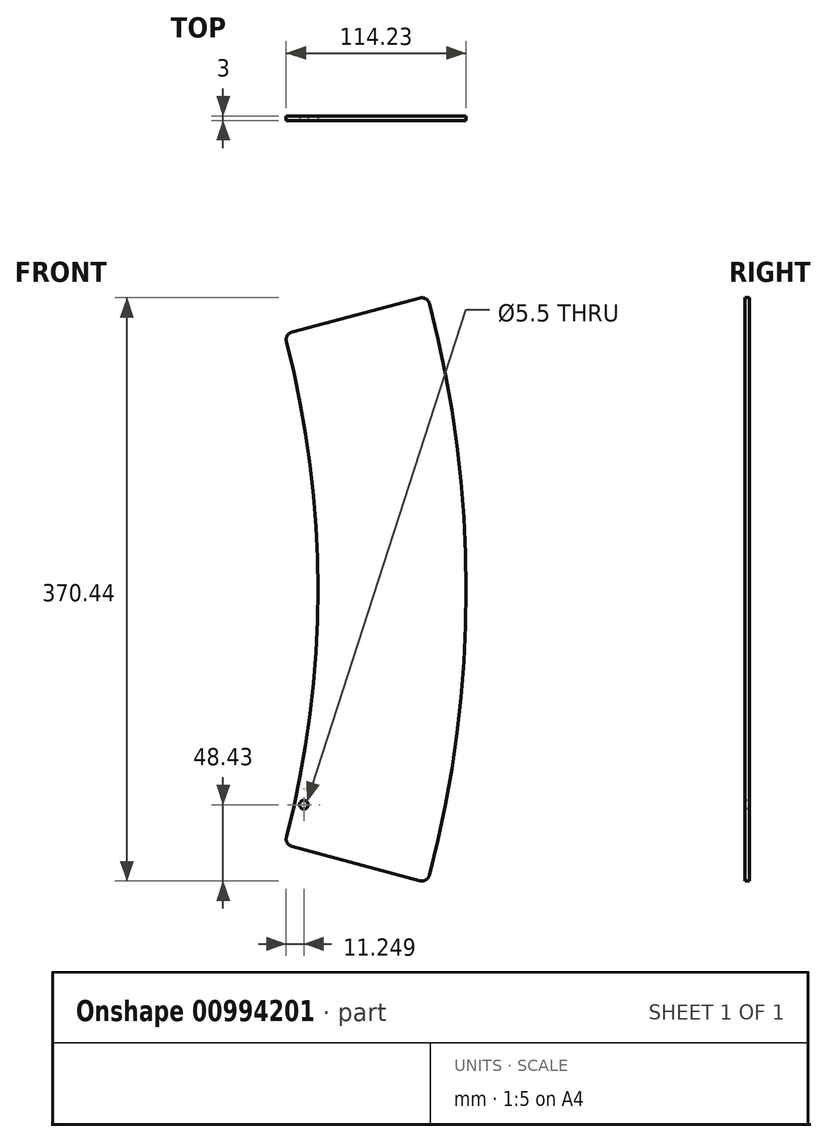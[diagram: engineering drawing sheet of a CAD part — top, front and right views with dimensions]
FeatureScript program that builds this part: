
annotation { "Feature Type Name" : "Feature", "Feature Type Description" : "" }
export const myFeature = defineFeature(function(context is Context, id is Id, definition is map)
    precondition{}
    {
        {
            var Q0;
            Q0=qCreatedBy(makeId("Right.planeOp"),FACE);
            var sketch = newSketch(context, id + "F0", { "sketchPlane" : qUnion([Q0])});
            skLineSegment(sketch, "E0", {"start": v(0, 0) * mm, "end": v(-93.97, 0) * mm});
            skSolve(sketch);
        }
        {
            var Q0;
            Q0=qCreatedBy(makeId("Front.planeOp"),FACE);
            var sketch = newSketch(context, id + "F1", { "sketchPlane" : qUnion([Q0])});
            skArc(sketch, "E1", {"start": v(695.47, -186.35) * mm, "mid": v(720, 0) * mm, "end": v(695.47, 186.35) * mm});
            skArc(sketch, "E2", {"start": v(604.67, -162.02) * mm, "mid": v(626, 0) * mm, "end": v(604.67, 162.02) * mm});
            skLineSegment(sketch, "E3", {"start": v(0, 0) * mm, "end": v(695.47, -186.35) * mm, "construction": true});
            skLineSegment(sketch, "E4", {"start": v(0, 0) * mm, "end": v(695.47, 186.35) * mm, "construction": true});
            skLineSegment(sketch, "E5", {"start": v(604.67, 162.02) * mm, "end": v(695.47, 186.35) * mm});
            skLineSegment(sketch, "E6", {"start": v(604.67, -162.02) * mm, "end": v(695.47, -186.35) * mm});
            skSolve(sketch);
        }
        {
            var Q0;
            Q0=makeQuery(id+"F1.imprint","IMPRINT",FACE,{"disambiguationData":[TD([[makeQuery(id+"F1.imprint","IMPRINT",EDGE,{"derivedFrom":sQuery(id+"F1.wireOp",EDGE,"E1")}),1.0]])]});
            extrude(context, id + "F2", {"entities" : qUnion([Q0]), "oppositeDirection" : true, "depth" : 3 * mm, "offsetDistance" : 25 * mm});
        }
        {
            var Q0;
            Q0=qCreatedBy(makeId("Front.planeOp"),FACE);
            var sketch = newSketch(context, id + "F3", { "sketchPlane" : qUnion([Q0])});
            skLineSegment(sketch, "E7", {"start": v(0, 0) * mm, "end": v(617.02, -136.79) * mm, "construction": true});
            skPoint(sketch, "E8", {"position": v(617.02, -136.79) * mm});
            skSolve(sketch);
        }
        {
            var Q0;
            Q0=sQuery(id+"F3.wireOp",VERTEX,"E8");
            var Q1;
            Q1=makeQuery(id+"F2.opExtrude","SWEPT_BODY",BODY,{"disambiguationData":[OSD([sQuery(id+"F1.wireOp",EDGE,"E1"),sQuery(id+"F1.wireOp",EDGE,"E2"),sQuery(id+"F1.wireOp",EDGE,"E5"),sQuery(id+"F1.wireOp",EDGE,"E6")])]});
            hole(context, id + "F4", {"style" : HoleStyle.SIMPLE, "endStyle" : HoleEndStyle.THROUGH, "standardTappedOrClearance" : lookupTablePath({ "fit" : "Normal", "standard" : "ISO", "size" : "M5", "type" : "Clearance" }), "standardBlindInLast" : lookupTablePath({ "fit" : "Normal", "standard" : "ISO", "engagement" : "75%", "pitch" : "0.8 mm", "size" : "M5", "type" : "Clearance & tapped" }), "holeDiameter" : 5.5 * mm, "majorDiameter" : 5 * mm, "isTappedThrough" : true, "tappedDepth" : 12 * mm, "tapClearance" : 3, "locations" : qUnion([Q0]), "scope" : qUnion([Q1])});
        }
        {
            var Q0;
            Q0=makeQuery(id+"F2.opExtrude","SWEPT_EDGE",EDGE,{"disambiguationData":[OSD([sQuery(id+"F1.wireOp",EDGE,"E1"),sQuery(id+"F1.wireOp",EDGE,"E5")])]});
            var Q1;
            Q1=makeQuery(id+"F2.opExtrude","SWEPT_EDGE",EDGE,{"disambiguationData":[OSD([sQuery(id+"F1.wireOp",EDGE,"E2"),sQuery(id+"F1.wireOp",EDGE,"E5")])]});
            var Q2;
            Q2=makeQuery(id+"F2.opExtrude","SWEPT_EDGE",EDGE,{"disambiguationData":[OSD([sQuery(id+"F1.wireOp",EDGE,"E1"),sQuery(id+"F1.wireOp",EDGE,"E6")])]});
            var Q3;
            Q3=makeQuery(id+"F2.opExtrude","SWEPT_EDGE",EDGE,{"disambiguationData":[OSD([sQuery(id+"F1.wireOp",EDGE,"E2"),sQuery(id+"F1.wireOp",EDGE,"E6")])]});
            fillet(context, id + "F5", {"entities" : qUnion([Q0, Q1, Q2, Q3]), "radius" : 5 * mm, "tangentPropagation" : true, "allowEdgeOverflow" : false});
        }
    });
